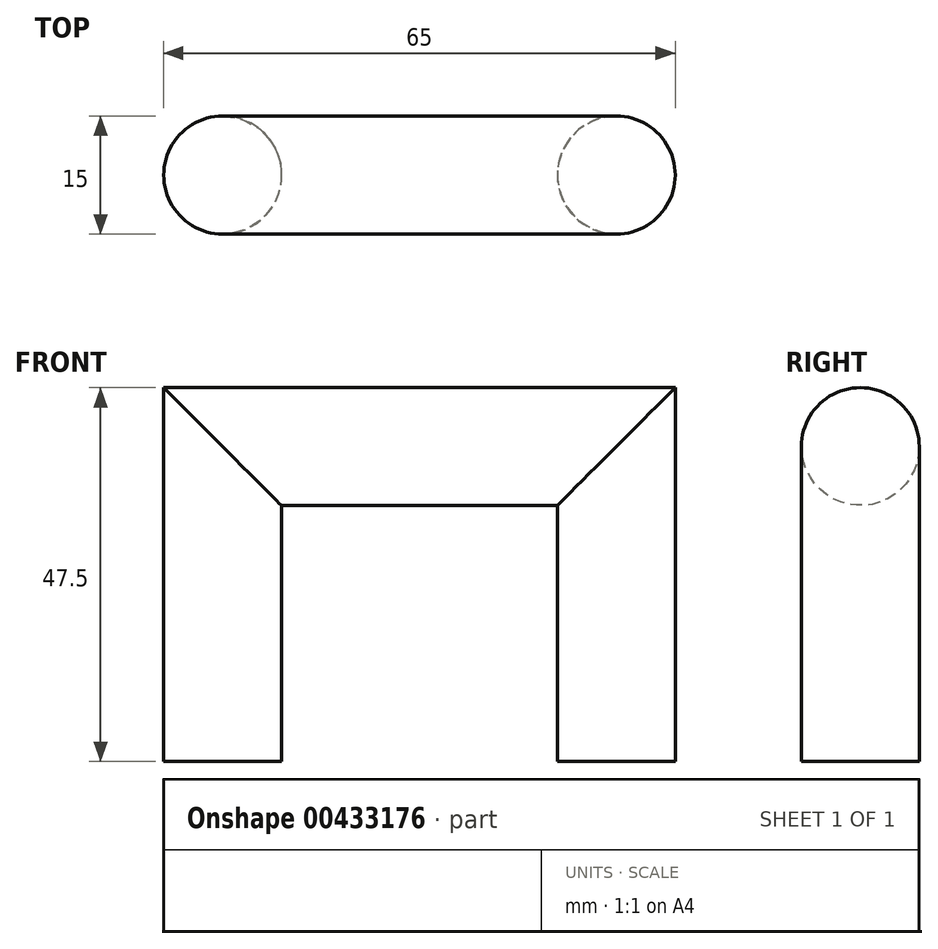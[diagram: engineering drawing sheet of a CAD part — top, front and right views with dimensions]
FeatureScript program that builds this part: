
annotation { "Feature Type Name" : "Feature", "Feature Type Description" : "" }
export const myFeature = defineFeature(function(context is Context, id is Id, definition is map)
    precondition{}
    {
        {
            var Q0;
            Q0=qCreatedBy(makeId("Front.planeOp"),FACE);
            var sketch = newSketch(context, id + "F0", { "sketchPlane" : qUnion([Q0])});
            skLineSegment(sketch, "E0", {"start": v(-25, 40) * mm, "end": v(25, 40) * mm});
            skLineSegment(sketch, "E1", {"start": v(25, 40) * mm, "end": v(25, 0) * mm});
            skLineSegment(sketch, "E2", {"start": v(-25, 40) * mm, "end": v(-25, 0) * mm});
            skSolve(sketch);
        }
        {
            var Q0;
            Q0=qCreatedBy(makeId("Top.planeOp"),FACE);
            var sketch = newSketch(context, id + "F1", { "sketchPlane" : qUnion([Q0])});
            skCircle(sketch, "E3", {"center": v(25, 0) * mm, "radius": 7.5 * mm});
            skSolve(sketch);
        }
        {
            var Q0;
            Q0=makeQuery(id+"F1.imprint","IMPRINT",FACE,{"disambiguationData":[TD([[makeQuery(id+"F1.imprint","IMPRINT",EDGE,{"derivedFrom":sQuery(id+"F1.wireOp",EDGE,"E3")}),1.0]])]});
            var Q1;
            Q1=sQuery(id+"F0.wireOp",EDGE,"E1");
            var Q2;
            Q2=sQuery(id+"F0.wireOp",EDGE,"E0");
            var Q3;
            Q3=sQuery(id+"F0.wireOp",EDGE,"E2");
            sweep(context, id + "F2", {"profiles" : qUnion([Q0]), "path" : qUnion([Q1, Q2, Q3])});
        }
    });
